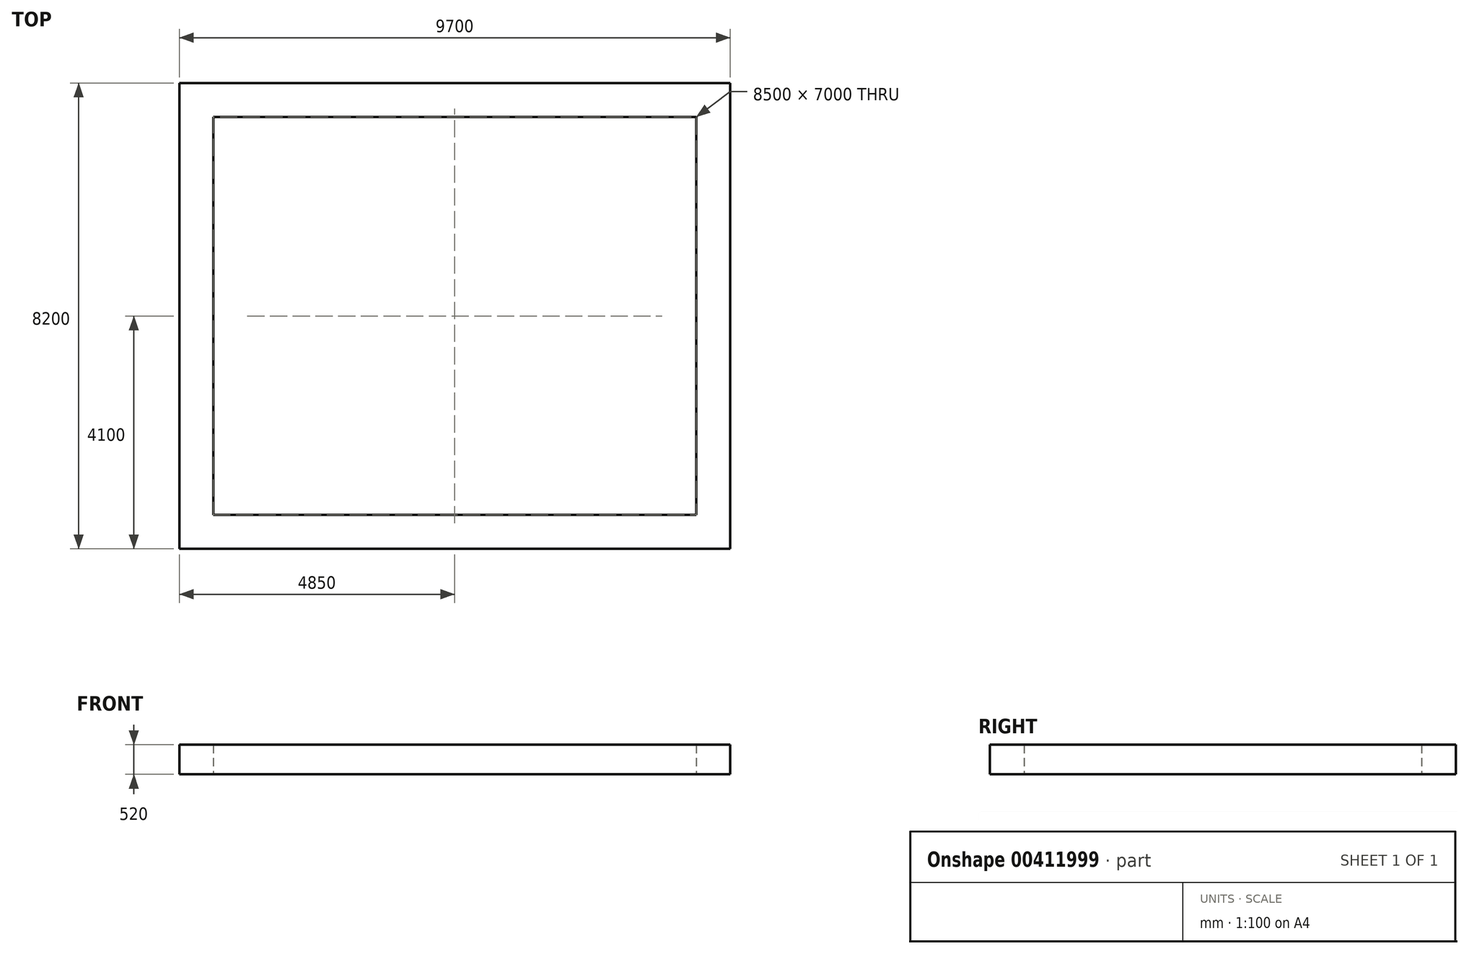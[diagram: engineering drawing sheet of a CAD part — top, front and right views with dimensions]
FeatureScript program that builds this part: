
annotation { "Feature Type Name" : "Feature", "Feature Type Description" : "" }
export const myFeature = defineFeature(function(context is Context, id is Id, definition is map)
    precondition{}
    {
        {
            var Q0;
            Q0=qCreatedBy(makeId("Top.planeOp"),FACE);
            var sketch = newSketch(context, id + "F0", { "sketchPlane" : qUnion([Q0])});
            skLineSegment(sketch, "E0.bottom", {"start": v(0, 0) * mm, "end": v(8500, 0) * mm});
            skLineSegment(sketch, "E0.top", {"start": v(0, 7000) * mm, "end": v(8500, 7000) * mm});
            skLineSegment(sketch, "E0.left", {"start": v(0, 0) * mm, "end": v(0, 7000) * mm});
            skLineSegment(sketch, "E0.right", {"start": v(8500, 0) * mm, "end": v(8500, 7000) * mm});
            skSolve(sketch);
        }
        {
            var Q0;
            Q0=qSketchRegion(id+"F0",true);
            extrude(context, id + "F1", {"entities" : qUnion([Q0]), "depth" : 520 * mm});
        }
        {
            var Q0;
            Q0=qCreatedBy(makeId("Top.planeOp"),FACE);
            var sketch = newSketch(context, id + "F2", { "sketchPlane" : qUnion([Q0])});
            skLineSegment(sketch, "E1.bottom", {"start": v(0, 7000) * mm, "end": v(8500, 7000) * mm});
            skLineSegment(sketch, "E1.top", {"start": v(0, 0) * mm, "end": v(8500, 0) * mm});
            skLineSegment(sketch, "E1.left", {"start": v(0, 7000) * mm, "end": v(0, 0) * mm});
            skLineSegment(sketch, "E1.right", {"start": v(8500, 7000) * mm, "end": v(8500, 0) * mm});
            skLineSegment(sketch, "E2.bottom", {"start": v(-600, 7600) * mm, "end": v(9100, 7600) * mm});
            skLineSegment(sketch, "E2.top", {"start": v(-600, -600) * mm, "end": v(9100, -600) * mm});
            skLineSegment(sketch, "E2.left", {"start": v(-600, 7600) * mm, "end": v(-600, -600) * mm});
            skLineSegment(sketch, "E2.right", {"start": v(9100, 7600) * mm, "end": v(9100, -600) * mm});
            skSolve(sketch);
        }
        {
            var Q0;
            Q0=qSketchRegion(id+"F2",true);
            var Q1;
            Q1=makeQuery(id+"F1.opExtrude","CAP_FACE",FACE,{"disambiguationData":[OSD([sQuery(id+"F0.wireOp",EDGE,"E0.bottom"),sQuery(id+"F0.wireOp",EDGE,"E0.top"),sQuery(id+"F0.wireOp",EDGE,"E0.left"),sQuery(id+"F0.wireOp",EDGE,"E0.right")])],"isStart":false});
            extrude(context, id + "F3", {"entities" : qUnion([Q0]), "endBound" : BoundingType.UP_TO_SURFACE, "endBoundEntityFace" : qUnion([Q1]), "depth" : 25 * mm});
        }
    });
